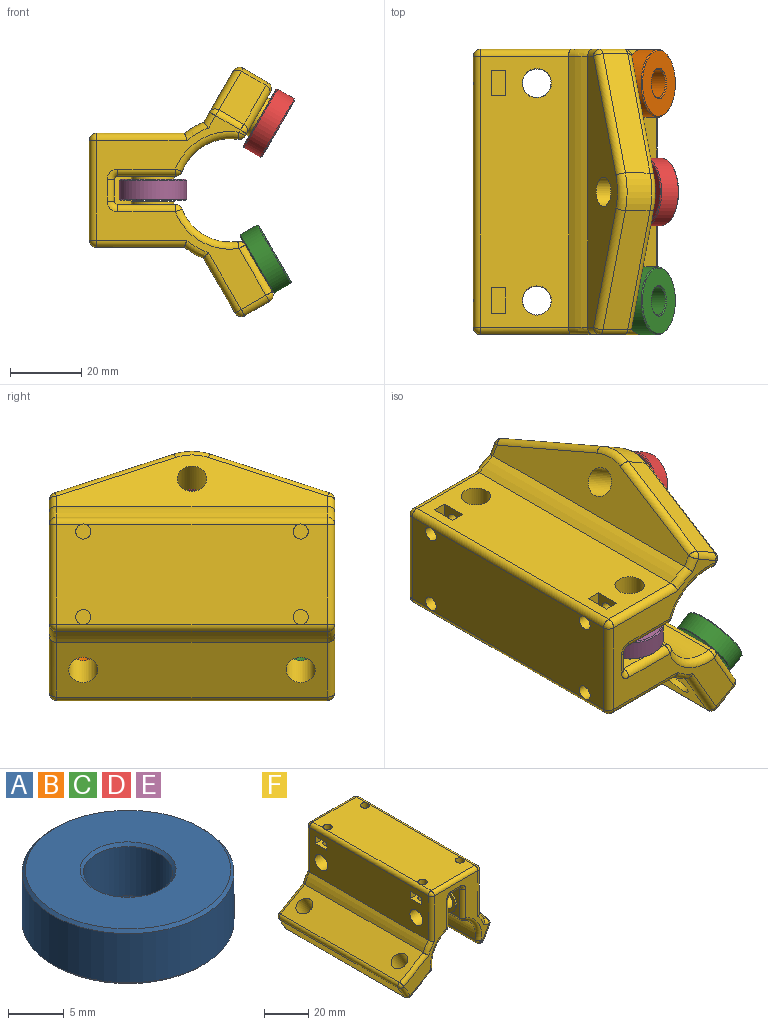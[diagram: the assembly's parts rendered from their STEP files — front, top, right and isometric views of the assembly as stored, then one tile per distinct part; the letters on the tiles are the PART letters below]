
ASSEMBLY  parts=6 mates=5
PART A: 8 faces, bbox 19x19x6 mm
  f0: cylinder r=4mm len=8mm, axis (0,0,-1), area 135.7mm2, adj f4,f6
  f1: cylinder r=9.5mm len=19mm, axis (0,0,-1), area 322.3mm2, adj f5,f7
  f2: plane 18.4x18.4mm, normal (0,0,1), area 207.8mm2, adj f6,f7
  f3: plane 18.4x18.4mm, normal (0,0,-1), area 207.8mm2, adj f4,f5
  f4: cone r=4.3mm half-angle=45deg, axis (0,0,-1), area 11.1mm2, adj f0,f3
  f5: cone r=9.5mm half-angle=45deg, axis (0,0,1), area 24.9mm2, adj f1,f3
  f6: cone r=4mm half-angle=45deg, axis (0,0,1), area 11.1mm2, adj f0,f2
  f7: cone r=9.2mm half-angle=45deg, axis (0,0,-1), area 24.9mm2, adj f1,f2
PART B: same geometry as A
PART C: same geometry as A
PART D: same geometry as A
PART E: same geometry as A
PART F: 155 faces, bbox 70.9x80x51.6 mm
  f0: plane 54.37x47.54mm, normal (0,1,0), area 620.3mm2, adj f104,f108,f112,f114,f115,f117,f118,f119
  f1: plane 54.37x47.54mm, normal (0,-1,0), area 620.3mm2, adj f83,f84,f86,f87,f88,f89,f90,f91
  f2: plane 76x28mm, normal (0,0,1), area 2071.7mm2, adj f67,f68,f73,f74,f97,f124,f144,f147
  f3: plane 76x24.66mm, normal (-1,0,0), area 1710.7mm2, adj f14,f24,f25,f55,f56,f57,f58,f60
  f4: plane 76x24.71mm, normal (1,0,0), area 1714.8mm2, adj f13,f22,f23,f45,f46,f47,f48,f50
  f5: plane 24.58x6mm, normal (0,0,-1), area 147.5mm2, adj f6,f31,f32,f88
  f6: cylinder r=1mm len=25.13mm, axis (0,-1,0), area 38.9mm2, adj f5,f8,f32,f90
  f7: cylinder r=1mm len=25.13mm, axis (0,1,0), area 38.9mm2, adj f9,f17,f32,f119
  f8: plane 76x16.13mm, normal (1,0,0), area 866.6mm2, adj f6,f27,f30,f32,f41,f43,f92,f112
  f9: plane 76x16.13mm, normal (-1,0,0), area 866.6mm2, adj f7,f28,f31,f32,f37,f39,f84,f121
  f10: plane 76x15.34mm, normal (-0.5,0,0.87), area 1240.4mm2, adj f14,f20,f21,f105,f113,f118
  f11: plane 76x13.11mm, normal (0.5,0,-0.87), area 924.3mm2, adj f26,f33,f35,f100,f107,f108
  f12: plane 76x14.41mm, normal (0.5,0,0.87), area 734.6mm2, adj f13,f77,f91,f130,f134,f135,f136
  f13: cylinder r=20.5mm len=76mm, axis (0,1,0), area 472.9mm2, adj f4,f12,f93,f128
  f14: cylinder r=20.5mm len=76mm, axis (0,1,0), area 472.9mm2, adj f3,f10,f101,f120
  f15: plane 76x6.93mm, normal (-0.87,0,-0.5), area 608mm2, adj f106,f107,f113,f114
  f16: cylinder r=14.5mm len=76mm, axis (0,1,0), area 1486.2mm2, adj f26,f27,f96,f104
  f17: plane 24.58x6mm, normal (0,0,-1), area 147.5mm2, adj f7,f30,f32,f117
  f18: cylinder r=14.5mm len=76mm, axis (0,1,0), area 1489.3mm2, adj f28,f29,f83,f125
  f19: plane 76x12.21mm, normal (-0.5,0,-0.87), area 481.5mm2, adj f29,f78,f87,f129,f139,f140,f141
  f20: cylinder r=4.1mm len=15.36mm, axis (-0.5,0,0.87), area 334.9mm2, adj f10,f36
  f21: cylinder r=4.1mm len=15.36mm, axis (-0.5,0,0.87), area 334.9mm2, adj f10,f34
  f22: cylinder r=4.1mm len=12.85mm, axis (1,0,0), area 331mm2, adj f4,f40
  f23: cylinder r=4.1mm len=12.85mm, axis (1,0,0), area 331mm2, adj f4,f38
  f24: cylinder r=4.1mm len=12.85mm, axis (1,0,0), area 331mm2, adj f3,f44
  f25: cylinder r=4.1mm len=12.85mm, axis (1,0,0), area 331mm2, adj f3,f42
  f26: cylinder r=2mm len=76mm, axis (0,1,0), area 182mm2, adj f11,f16,f98,f103
  f27: cylinder r=2mm len=76mm, axis (0,1,0), area 182.2mm2, adj f8,f16,f94,f109
  f28: cylinder r=2mm len=76mm, axis (0,1,0), area 182.2mm2, adj f9,f18,f82,f123
  f29: cylinder r=2mm len=76mm, axis (0,1,0), area 182.4mm2, adj f18,f19,f85,f127
  f30: cylinder r=1mm len=25.13mm, axis (0,-1,0), area 38.9mm2, adj f8,f17,f32,f115
  f31: cylinder r=1mm len=25.13mm, axis (0,1,0), area 38.9mm2, adj f5,f9,f32,f86
  f32: cylinder r=15mm len=26.84mm, axis (1,0,0), area 264.9mm2, adj f5,f6,f7,f8,f9,f17,f30,f31
  f33: cylinder r=6mm len=12mm, axis (-0.5,0,0.87), area 37.7mm2, adj f11,f34
  f34: plane 12x10.39mm, normal (0.5,0,-0.87), area 60.3mm2, adj f21,f33
  f35: cylinder r=6mm len=12mm, axis (-0.5,0,0.87), area 37.7mm2, adj f11,f36
  f36: plane 12x10.39mm, normal (0.5,0,-0.87), area 60.3mm2, adj f20,f35
  f37: cylinder r=6mm len=12mm, axis (1,0,0), area 31.2mm2, adj f9,f38
  f38: plane 12x12mm, normal (-1,0,0), area 60.3mm2, adj f23,f37
  f39: cylinder r=6mm len=12mm, axis (1,0,0), area 31.2mm2, adj f9,f40
  f40: plane 12x12mm, normal (-1,0,0), area 60.3mm2, adj f22,f39
  f41: cylinder r=6mm len=12mm, axis (-1,0,0), area 32.9mm2, adj f8,f42
  f42: plane 12x12mm, normal (1,0,0), area 60.3mm2, adj f25,f41
  f43: cylinder r=6mm len=12mm, axis (-1,0,0), area 32.9mm2, adj f8,f44
  f44: plane 12x12mm, normal (1,0,0), area 60.3mm2, adj f24,f43
  f45: plane 8x4mm, normal (0,1,0), area 32mm2, adj f4,f46,f48,f49
  f46: plane 8x7.2mm, normal (0,0,1), area 43.4mm2, adj f4,f45,f47,f49,f75
  f47: plane 8x4mm, normal (0,-1,0), area 32mm2, adj f4,f46,f48,f49
  f48: plane 8x7.2mm, normal (0,0,-1), area 43.4mm2, adj f4,f45,f47,f49,f74
  f49: plane 7.2x4mm, normal (1,0,0), area 28.8mm2, adj f45,f46,f47,f48
  f50: plane 8x7.2mm, normal (0,0,-1), area 43.4mm2, adj f4,f51,f53,f54,f73
  f51: plane 8x4mm, normal (0,1,0), area 32mm2, adj f4,f50,f52,f54
  f52: plane 8x7.2mm, normal (0,0,1), area 43.4mm2, adj f4,f51,f53,f54,f72
  f53: plane 8x4mm, normal (0,-1,0), area 32mm2, adj f4,f50,f52,f54
  f54: plane 7.2x4mm, normal (1,0,0), area 28.8mm2, adj f50,f51,f52,f53
  f55: plane 8x7.2mm, normal (0,0,1), area 43.4mm2, adj f3,f56,f58,f59,f69
  f56: plane 8x4mm, normal (0,1,0), area 32mm2, adj f3,f55,f57,f59
  f57: plane 8x7.2mm, normal (0,0,-1), area 43.4mm2, adj f3,f56,f58,f59,f68
  f58: plane 8x4mm, normal (0,-1,0), area 32mm2, adj f3,f55,f57,f59
  f59: plane 7.2x4mm, normal (-1,0,0), area 28.8mm2, adj f55,f56,f57,f58
  f60: plane 8x7.2mm, normal (0,0,-1), area 43.4mm2, adj f3,f61,f63,f64,f67
  f61: plane 8x4mm, normal (0,-1,0), area 32mm2, adj f3,f60,f62,f64
  f62: plane 8x7.2mm, normal (0,0,1), area 43.4mm2, adj f3,f61,f63,f64,f66
  f63: plane 8x4mm, normal (0,1,0), area 32mm2, adj f3,f60,f62,f64
  f64: plane 7.2x4mm, normal (-1,0,0), area 28.8mm2, adj f60,f61,f62,f63
  f65: plane 4.25x4.25mm, normal (0,0,1), area 14.2mm2, adj f66
  f66: cylinder r=2.12mm len=4.25mm, axis (0,0,1), area 53.4mm2, adj f62,f65
  f67: cylinder r=2.12mm len=5mm, axis (0,0,1), area 66.8mm2, adj f2,f60,f147
  f68: cylinder r=2.12mm len=5mm, axis (0,0,1), area 66.8mm2, adj f2,f57,f147
  f69: cylinder r=2.12mm len=4.25mm, axis (0,0,1), area 53.4mm2, adj f55,f70
  f70: plane 4.25x4.25mm, normal (0,0,1), area 14.2mm2, adj f69
  f71: plane 4.25x4.25mm, normal (0,0,1), area 14.2mm2, adj f72
  f72: cylinder r=2.12mm len=4.25mm, axis (0,0,1), area 53.4mm2, adj f52,f71
  f73: cylinder r=2.12mm len=5mm, axis (0,0,1), area 66.8mm2, adj f2,f50,f144
  f74: cylinder r=2.12mm len=5mm, axis (0,0,1), area 66.8mm2, adj f2,f48,f144
  f75: cylinder r=2.12mm len=4.25mm, axis (0,0,1), area 53.4mm2, adj f46,f76
  f76: plane 4.25x4.25mm, normal (0,0,1), area 14.2mm2, adj f75
  f77: cylinder r=4.1mm len=15.36mm, axis (0.5,0,0.87), area 334.9mm2, adj f12,f79
  f78: cylinder r=6mm len=12mm, axis (0.5,0,0.87), area 37.7mm2, adj f19,f79
  f79: plane 12x10.39mm, normal (-0.5,0,-0.87), area 60.3mm2, adj f77,f78
  f80: plane 33.44x14.86mm, normal (0.81,-0.35,-0.47), area 285.7mm2, adj f89,f132,f134,f139
  f81: plane 33.44x14.86mm, normal (0.81,0.35,-0.47), area 285.7mm2, adj f131,f132,f136,f141
  f82: sphere r=2mm, area 4.8mm2, adj f28,f83,f84
  f83: torus R=16.5mm, axis (0,-1,0), area 64.6mm2, adj f1,f18,f82,f85
  f84: cylinder r=2mm len=16.13mm, axis (0,0,1), area 50.7mm2, adj f1,f9,f82,f86
  f85: sphere r=2mm, area 4.8mm2, adj f29,f83,f87
  f86: torus R=3mm, axis (0,-1,0), area 8.5mm2, adj f1,f31,f84,f88
  f87: cylinder r=2mm len=2.1mm, axis (-0.87,0,0.5), area 2.3mm2, adj f1,f19,f85,f138
  f88: cylinder r=2mm len=6mm, axis (-1,0,0), area 18.8mm2, adj f1,f5,f86,f90
  f89: cylinder r=2mm len=7.86mm, axis (-0.5,0,-0.87), area 19.4mm2, adj f1,f80,f133,f138
  f90: torus R=3mm, axis (0,-1,0), area 8.5mm2, adj f1,f6,f88,f92
  f91: cylinder r=2mm len=4.46mm, axis (0.87,0,-0.5), area 11.1mm2, adj f1,f12,f93,f133
  f92: cylinder r=2mm len=16.13mm, axis (0,0,-1), area 50.7mm2, adj f1,f8,f90,f94
  f93: torus R=18.5mm, axis (0,-1,0), area 20.4mm2, adj f1,f13,f91,f95
  f94: sphere r=2mm, area 4.8mm2, adj f27,f92,f96
  f95: cylinder r=2mm len=25.43mm, axis (0,0,-1), area 78.4mm2, adj f1,f4,f93,f145
  f96: torus R=16.5mm, axis (0,-1,0), area 64.5mm2, adj f1,f16,f94,f98
  f97: cylinder r=2mm len=28mm, axis (1,0,0), area 88mm2, adj f1,f2,f145,f148
  f98: sphere r=2mm, area 4.8mm2, adj f26,f96,f100
  f99: cylinder r=2mm len=25.38mm, axis (0,0,1), area 78.3mm2, adj f1,f3,f101,f148
  f100: cylinder r=2mm len=14.11mm, axis (-0.87,0,-0.5), area 47.6mm2, adj f1,f11,f98,f102
  f101: torus R=18.5mm, axis (0,-1,0), area 20.4mm2, adj f1,f14,f99,f105
  f102: sphere r=2mm, area 6.3mm2, adj f100,f106,f107
  f103: sphere r=2mm, area 4.8mm2, adj f26,f104,f108
  f104: torus R=16.5mm, axis (0,-1,0), area 64.5mm2, adj f0,f16,f103,f109
  f105: cylinder r=2mm len=16.96mm, axis (0.87,0,0.5), area 56.5mm2, adj f1,f10,f101,f110
  f106: cylinder r=2mm len=7.93mm, axis (-0.5,0,0.87), area 25.1mm2, adj f1,f15,f102,f110
  f107: cylinder r=2mm len=76mm, axis (0,1,0), area 238.8mm2, adj f11,f15,f102,f111
  f108: cylinder r=2mm len=14.11mm, axis (0.87,0,0.5), area 47.6mm2, adj f0,f11,f103,f111
  f109: sphere r=2mm, area 4.8mm2, adj f27,f104,f112
  f110: sphere r=2mm, area 6.3mm2, adj f105,f106,f113
  f111: sphere r=2mm, area 6.3mm2, adj f107,f108,f114
  f112: cylinder r=2mm len=16.13mm, axis (0,0,1), area 50.7mm2, adj f0,f8,f109,f115
  f113: cylinder r=2mm len=76mm, axis (0,1,0), area 238.8mm2, adj f10,f15,f110,f116
  f114: cylinder r=2mm len=7.93mm, axis (0.5,0,-0.87), area 25.1mm2, adj f0,f15,f111,f116
  f115: torus R=3mm, axis (0,-1,0), area 8.5mm2, adj f0,f30,f112,f117
  f116: sphere r=2mm, area 6.3mm2, adj f113,f114,f118
  f117: cylinder r=2mm len=6mm, axis (1,0,0), area 18.8mm2, adj f0,f17,f115,f119
  f118: cylinder r=2mm len=16.96mm, axis (-0.87,0,-0.5), area 56.5mm2, adj f0,f10,f116,f120
  f119: torus R=3mm, axis (0,-1,0), area 8.5mm2, adj f0,f7,f117,f121
  f120: torus R=18.5mm, axis (0,-1,0), area 20.4mm2, adj f0,f14,f118,f122
  f121: cylinder r=2mm len=16.13mm, axis (0,0,-1), area 50.7mm2, adj f0,f9,f119,f123
  f122: cylinder r=2mm len=25.38mm, axis (0,0,-1), area 78.3mm2, adj f0,f3,f120,f146
  f123: sphere r=2mm, area 4.8mm2, adj f28,f121,f125
  f124: cylinder r=2mm len=28mm, axis (-1,0,0), area 88mm2, adj f0,f2,f143,f146
  f125: torus R=16.5mm, axis (0,-1,0), area 64.6mm2, adj f0,f18,f123,f127
  f126: cylinder r=2mm len=25.43mm, axis (0,0,1), area 78.4mm2, adj f0,f4,f128,f143
  f127: sphere r=2mm, area 4.8mm2, adj f29,f125,f129
  f128: torus R=18.5mm, axis (0,-1,0), area 20.4mm2, adj f0,f13,f126,f130
  f129: cylinder r=2mm len=2.1mm, axis (0.87,0,-0.5), area 2.3mm2, adj f0,f19,f127,f142
  f130: cylinder r=2mm len=4.46mm, axis (-0.87,0,0.5), area 11.1mm2, adj f0,f12,f128,f137
  f131: cylinder r=2mm len=7.86mm, axis (0.5,0,0.87), area 19.4mm2, adj f0,f81,f137,f142
  f132: cylinder r=15mm len=10.53mm, axis (0.5,0,0.87), area 86.1mm2, adj f80,f81,f135,f140
  f133: sphere r=2mm, area 4.8mm2, adj f89,f91,f134
  f134: cylinder r=2mm len=34.14mm, axis (0.3,0.94,-0.18), area 112.2mm2, adj f12,f80,f133,f135
  f135: torus R=13mm, axis (0.5,0,0.87), area 32.2mm2, adj f12,f132,f134,f136
  f136: cylinder r=2mm len=34.14mm, axis (-0.3,0.94,0.18), area 112.2mm2, adj f12,f81,f135,f137
  f137: sphere r=2mm, area 4.8mm2, adj f130,f131,f136
  f138: sphere r=2mm, area 4.8mm2, adj f87,f89,f139
  f139: cylinder r=2mm len=34.14mm, axis (-0.3,-0.94,0.18), area 112.2mm2, adj f19,f80,f138,f140
  f140: torus R=13mm, axis (0.5,0,0.87), area 32.2mm2, adj f19,f132,f139,f141
  f141: cylinder r=2mm len=34.14mm, axis (0.3,-0.94,-0.18), area 112.2mm2, adj f19,f81,f140,f142
  f142: sphere r=2mm, area 4.8mm2, adj f129,f131,f141
  f143: sphere r=2mm, area 6.3mm2, adj f124,f126,f144
  f144: cylinder r=2mm len=76mm, axis (0,1,0), area 238.5mm2, adj f2,f4,f73,f74,f143,f145
  f145: sphere r=2mm, area 6.3mm2, adj f95,f97,f144
  f146: sphere r=2mm, area 6.3mm2, adj f122,f124,f147
  f147: cylinder r=2mm len=76mm, axis (0,1,0), area 238.5mm2, adj f2,f3,f67,f68,f146,f148
  f148: sphere r=2mm, area 6.3mm2, adj f97,f99,f147
  f149: cylinder r=12.5mm len=21.11mm, axis (1,0,0), area 200mm2, adj f150,f151,f152,f153,f154
  f150: cylinder r=1mm len=21.11mm, axis (0,1,0), area 32.4mm2, adj f149,f152,f153
  f151: cylinder r=1mm len=21.11mm, axis (0,-1,0), area 32.4mm2, adj f149,f152,f154
  f152: plane 21.11x6mm, normal (0,0,-1), area 126.6mm2, adj f149,f150,f151
  f153: plane 19.7x4.8mm, normal (-1,0,0), area 66mm2, adj f149,f150
  f154: plane 19.7x4.8mm, normal (1,0,0), area 66mm2, adj f149,f151
PLACE A t=(71.04,87.1,65.75)mm
PLACE B rot(axis=(0,-1,0),120deg) t=(105.31,87.1,50.77)mm
PLACE C rot(axis=(0,-1,0),120deg) t=(105.31,26.1,50.77)mm
PLACE D rot(axis=(0,-1,0),60deg) t=(106.24,56.6,85.91)mm
PLACE E t=(71.04,26.1,65.75)mm
PLACE F rot(axis=(0,-1,0),90deg) t=(121.27,56.6,3.69)mm
MATE fastened F.f23 <-> E.f1  axis (0,0,-1) through (71.04,26.1,71.75)mm
MATE fastened F.f77 <-> D.f0  axis (0.87,0,-0.5) through (101.04,56.6,88.91)mm
MATE fastened F.f21 <-> B.f1  axis (0.87,0,0.5) through (100.11,87.1,47.77)mm
MATE fastened F.f20 <-> C.f1  axis (0.87,0,0.5) through (100.11,26.1,47.77)mm
MATE fastened F.f22 <-> A.f1  axis (0,0,-1) through (71.04,87.1,71.75)mm
